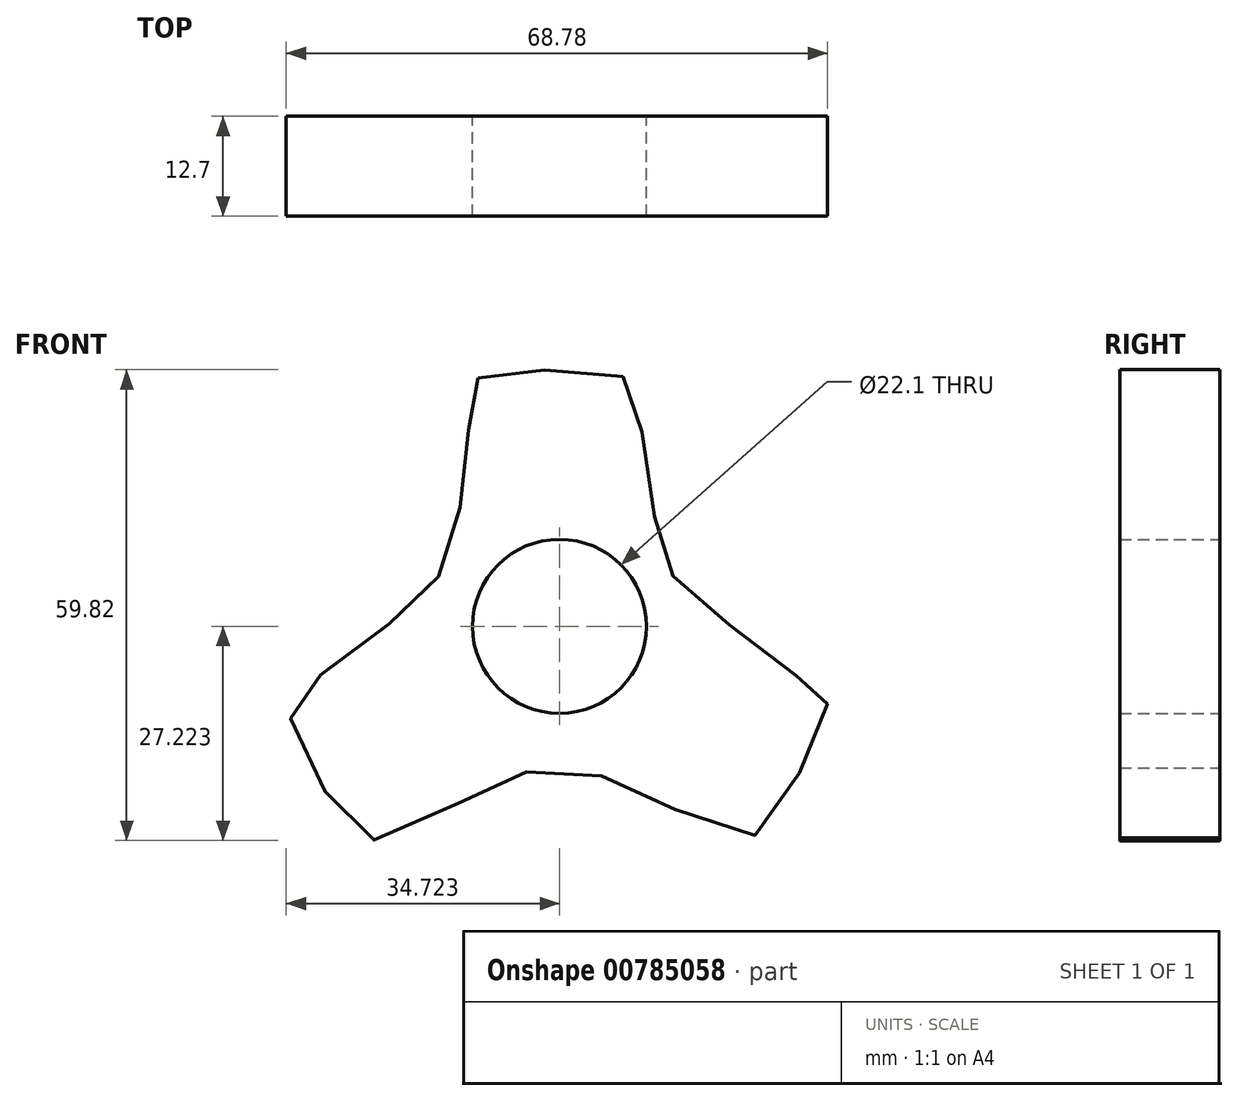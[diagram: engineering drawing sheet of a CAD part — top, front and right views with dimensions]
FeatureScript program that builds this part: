
annotation { "Feature Type Name" : "Feature", "Feature Type Description" : "" }
export const myFeature = defineFeature(function(context is Context, id is Id, definition is map)
    precondition{}
    {
        {
            var Q0;
            Q0=qCreatedBy(makeId("Front.planeOp"),FACE);
            var sketch = newSketch(context, id + "F0", { "sketchPlane" : qUnion([Q0])});
            skFitSpline(sketch, "E0", {"points": [v(-48.43, 72.49) * mm, v(-45.39, 73.02) * mm, v(-39.43, 73.55) * mm, v(-34, 73.15) * mm, v(-28.59, 72.49) * mm, v(-28.45, 72.36) * mm, v(-27.66, 66.14) * mm, v(-26.6, 58.6) * mm, v(-25.54, 52.25) * mm, v(-24.88, 49.47) * mm, v(-21.84, 45.24) * mm, v(-17.34, 41.8) * mm, v(-12.31, 37.96) * mm, v(-6.76, 33.86) * mm, v(-5.04, 32.8) * mm, v(-4.11, 32.14) * mm, v(-4.38, 29.76) * mm, v(-6.5, 24.47) * mm, v(-10.46, 17.72) * mm, v(-13.24, 14.41) * mm, v(-14.43, 14.15) * mm, v(-25.15, 18.52) * mm, v(-30.7, 21.16) * mm, v(-35.86, 22.75) * mm, v(-41.81, 22.62) * mm, v(-46.84, 20.37) * mm, v(-53.2, 17.46) * mm, v(-61.4, 13.89) * mm, v(-62.45, 13.89) * mm, v(-66.82, 18.52) * mm, v(-70.52, 25) * mm, v(-72.5, 30.02) * mm, v(-72.64, 31.61) * mm, v(-68.27, 34.92) * mm, v(-62.58, 39.15) * mm, v(-56.76, 43.65) * mm, v(-54.12, 46.43) * mm, v(-51.87, 50.13) * mm, v(-50.68, 55.95) * mm, v(-49.88, 62.83) * mm, v(-49.49, 67.2) * mm, v(-49.09, 70.1) * mm, v(-48.43, 72.49) * mm]});
            skCircle(sketch, "E1", {"center": v(-38.06, 40.96) * mm, "radius": 11.05 * mm});
            skSolve(sketch);
        }
        {
            var Q0;
            Q0 = qSketchRegion(id + "F0", true);
            extrude(context, id + "F1", {"entities" : qUnion([Q0]), "depth" : 12.7 * mm, "offsetDistance" : 25.4 * mm});
        }
    });
